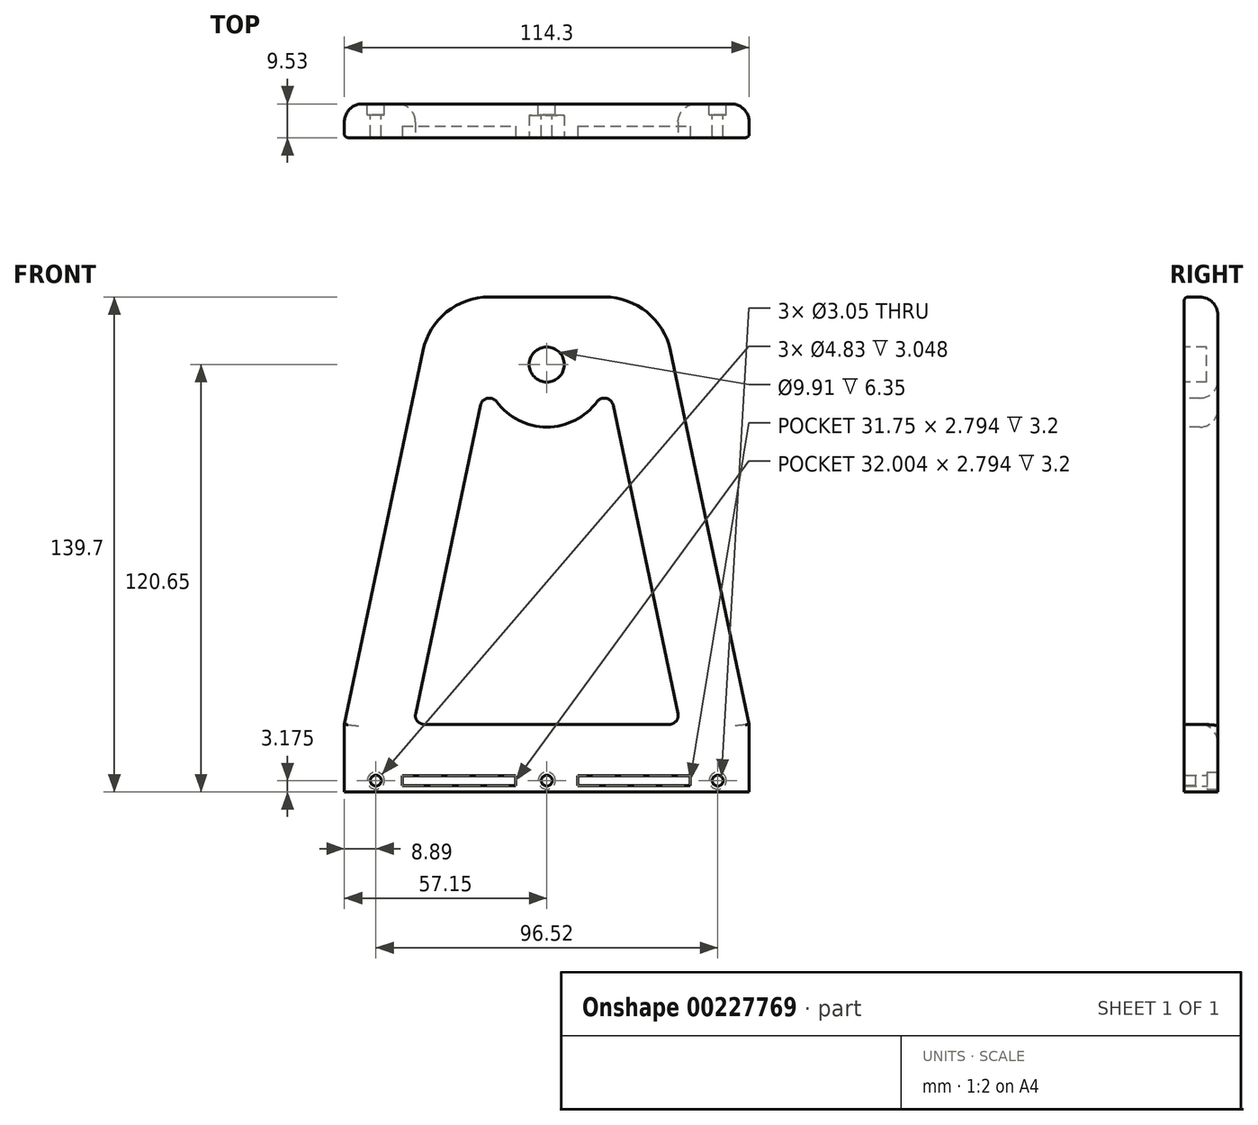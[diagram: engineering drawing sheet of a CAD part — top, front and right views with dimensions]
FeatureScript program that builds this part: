
annotation { "Feature Type Name" : "Feature", "Feature Type Description" : "" }
export const myFeature = defineFeature(function(context is Context, id is Id, definition is map)
    precondition{}
    {
        {
            var Q0;
            Q0=qCreatedBy(makeId("Front.planeOp"),FACE);
            var sketch = newSketch(context, id + "F0", { "sketchPlane" : qUnion([Q0])});
            skLineSegment(sketch, "E0", {"start": v(-57.15, 0) * mm, "end": v(57.15, 0) * mm});
            skLineSegment(sketch, "E1", {"start": v(57.15, 0) * mm, "end": v(57.15, 19.05) * mm});
            skLineSegment(sketch, "E2", {"start": v(57.15, 19.05) * mm, "end": v(31.75, 139.7) * mm});
            skLineSegment(sketch, "E3", {"start": v(31.75, 139.7) * mm, "end": v(-31.75, 139.7) * mm});
            skLineSegment(sketch, "E4", {"start": v(-57.15, 0) * mm, "end": v(-57.15, 19.05) * mm});
            skLineSegment(sketch, "E5", {"start": v(-57.15, 19.05) * mm, "end": v(-31.75, 139.7) * mm});
            skSolve(sketch);
        }
        {
            var Q0;
            Q0=qSketchRegion(id+"F0",true);
            extrude(context, id + "F1", {"entities" : qUnion([Q0]), "depth" : 9.52 * mm});
        }
        {
            var Q0;
            Q0=makeQuery(id+"F1.opExtrude","CAP_FACE",FACE,{"disambiguationData":[OSD([sQuery(id+"F0.wireOp",EDGE,"E0"),sQuery(id+"F0.wireOp",EDGE,"E1"),sQuery(id+"F0.wireOp",EDGE,"E2"),sQuery(id+"F0.wireOp",EDGE,"E3"),sQuery(id+"F0.wireOp",EDGE,"E4"),sQuery(id+"F0.wireOp",EDGE,"E5")])],"isStart":false});
            var sketch = newSketch(context, id + "F2", { "sketchPlane" : qUnion([Q0])});
            skCircle(sketch, "E6", {"center": v(0, 120.65) * mm, "radius": 4.95 * mm});
            skPoint(sketch, "E6.centerSnap0", {"position": v(0, 139.7) * mm});
            skSolve(sketch);
        }
        {
            var Q0;
            Q0=qSketchRegion(id+"F2",true);
            extrude(context, id + "F3", {"entities" : qUnion([Q0]), "operationType" : NewBodyOperationType.REMOVE, "oppositeDirection" : true, "depth" : 6.35 * mm});
        }
        {
            var Q0;
            Q0=makeQuery(id+"F1.opExtrude","SWEPT_EDGE",EDGE,{"disambiguationData":[OSD([sQuery(id+"F0.wireOp",EDGE,"E2"),sQuery(id+"F0.wireOp",EDGE,"E3")])]});
            var Q1;
            Q1=makeQuery(id+"F1.opExtrude","SWEPT_EDGE",EDGE,{"disambiguationData":[OSD([sQuery(id+"F0.wireOp",EDGE,"E3"),sQuery(id+"F0.wireOp",EDGE,"E5")])]});
            fillet(context, id + "F4", {"entities" : qUnion([Q0, Q1]), "radius" : 19.05 * mm, "tangentPropagation" : true, "allowEdgeOverflow" : false});
        }
        {
            var Q0;
            Q0=makeQuery(id+"F1.opExtrude","CAP_FACE",FACE,{"disambiguationData":[OSD([sQuery(id+"F0.wireOp",EDGE,"E0"),sQuery(id+"F0.wireOp",EDGE,"E1"),sQuery(id+"F0.wireOp",EDGE,"E2"),sQuery(id+"F0.wireOp",EDGE,"E3"),sQuery(id+"F0.wireOp",EDGE,"E4"),sQuery(id+"F0.wireOp",EDGE,"E5")])],"isStart":false});
            var sketch = newSketch(context, id + "F5", { "sketchPlane" : qUnion([Q0])});
            skArc(sketch, "E7", {"start": v(-14.19, 110.14) * mm, "mid": v(0, 103) * mm, "end": v(14.19, 110.14) * mm});
            skLineSegment(sketch, "E8", {"start": v(-34.55, 19.05) * mm, "end": v(34.55, 19.05) * mm});
            skLineSegment(sketch, "E9", {"start": v(37.04, 22.11) * mm, "end": v(18.71, 109.16) * mm});
            skLineSegment(sketch, "E10", {"start": v(-37.04, 22.11) * mm, "end": v(-18.71, 109.16) * mm});
            skPoint(sketch, "E11.visualSharp", {"position": v(-17.16, 116.52) * mm});
            skArc(sketch, "E11.filletArc", {"start": v(-14.19, 110.14) * mm, "mid": v(-16.77, 111.11) * mm, "end": v(-18.71, 109.16) * mm});
            skPoint(sketch, "E12.visualSharp", {"position": v(17.16, 116.52) * mm});
            skArc(sketch, "E12.filletArc", {"start": v(18.71, 109.16) * mm, "mid": v(16.77, 111.11) * mm, "end": v(14.19, 110.14) * mm});
            skPoint(sketch, "E13.visualSharp", {"position": v(37.68, 19.05) * mm});
            skArc(sketch, "E13.filletArc", {"start": v(34.55, 19.05) * mm, "mid": v(36.52, 19.99) * mm, "end": v(37.04, 22.11) * mm});
            skPoint(sketch, "E14.visualSharp", {"position": v(-37.68, 19.05) * mm});
            skArc(sketch, "E14.filletArc", {"start": v(-37.04, 22.11) * mm, "mid": v(-36.52, 19.99) * mm, "end": v(-34.55, 19.05) * mm});
            skSolve(sketch);
        }
        {
            var Q0;
            Q0=makeQuery(id+"F5.imprint","IMPRINT",FACE,{"disambiguationData":[TD([[makeQuery(id+"F5.imprint","IMPRINT",EDGE,{"derivedFrom":sQuery(id+"F5.wireOp",EDGE,"E7")}),-1.0]])]});
            extrude(context, id + "F6", {"entities" : qUnion([Q0]), "operationType" : NewBodyOperationType.REMOVE, "oppositeDirection" : true, "depth" : 25.4 * mm});
        }
        {
            var Q0;
            {var subQ0=sQuery(id+"F0.wireOp",EDGE,"E5");var subQ1=sQuery(id+"F0.wireOp",EDGE,"E3");Q0=makeQuery(id+"F4.opFillet","BLEND_EDGE",EDGE,{"blendedFrom":[makeQuery(id+"F1.opExtrude","SWEPT_EDGE",EDGE,{"disambiguationData":[OSD([subQ1,subQ0])]}),makeQuery(id+"F1.opExtrude","CAP_FACE",FACE,{"disambiguationData":[OSD([sQuery(id+"F0.wireOp",EDGE,"E0"),sQuery(id+"F0.wireOp",EDGE,"E1"),sQuery(id+"F0.wireOp",EDGE,"E2"),subQ1,sQuery(id+"F0.wireOp",EDGE,"E4"),subQ0])],"isStart":true})],"blendedInto":[makeQuery(id+"F1.opExtrude","CAP_FACE",FACE,{"disambiguationData":[OSD([sQuery(id+"F0.wireOp",EDGE,"E0"),sQuery(id+"F0.wireOp",EDGE,"E1"),sQuery(id+"F0.wireOp",EDGE,"E2"),subQ1,sQuery(id+"F0.wireOp",EDGE,"E4"),subQ0])],"isStart":true})]});}
            var Q1;
            Q1=makeQuery(id+"F1.opExtrude","CAP_EDGE",EDGE,{"disambiguationData":[OSD([sQuery(id+"F0.wireOp",EDGE,"E4")])],"isStart":true});
            var Q2;
            Q2=makeQuery(id+"F1.opExtrude","CAP_EDGE",EDGE,{"disambiguationData":[OSD([sQuery(id+"F0.wireOp",EDGE,"E1")])],"isStart":true});
            var Q3;
            Q3=makeQuery(id+"F6.boolean.opBoolean","INTERSECT",EDGE,{"derivedFrom":[makeQuery(id+"F1.opExtrude","CAP_FACE",FACE,{"disambiguationData":[OSD([sQuery(id+"F0.wireOp",EDGE,"E0"),sQuery(id+"F0.wireOp",EDGE,"E1"),sQuery(id+"F0.wireOp",EDGE,"E2"),sQuery(id+"F0.wireOp",EDGE,"E3"),sQuery(id+"F0.wireOp",EDGE,"E4"),sQuery(id+"F0.wireOp",EDGE,"E5")])],"isStart":true}),makeQuery(id+"F6.opExtrude","SWEPT_FACE",FACE,{"disambiguationData":[OSD([sQuery(id+"F5.wireOp",EDGE,"E7")])]})]});
            fillet(context, id + "F7", {"entities" : qUnion([Q0, Q1, Q2, Q3]), "radius" : 5.08 * mm, "tangentPropagation" : true, "allowEdgeOverflow" : false});
        }
        {
            var Q0;
            Q0=makeQuery(id+"F1.opExtrude","CAP_EDGE",EDGE,{"disambiguationData":[OSD([sQuery(id+"F0.wireOp",EDGE,"E1")])],"isStart":false});
            var Q1;
            Q1=makeQuery(id+"F1.opExtrude","CAP_EDGE",EDGE,{"disambiguationData":[OSD([sQuery(id+"F0.wireOp",EDGE,"E2")])],"isStart":false});
            var Q2;
            Q2=makeQuery(id+"F6.boolean.opBoolean","COPY",EDGE,{"derivedFrom":makeQuery(id+"F6.opExtrude","CAP_EDGE",EDGE,{"disambiguationData":[OSD([sQuery(id+"F5.wireOp",EDGE,"E10")])],"isStart":true})});
            var Q3;
            Q3=makeQuery(id+"F3.boolean.opBoolean","COPY",EDGE,{"derivedFrom":makeQuery(id+"F3.opExtrude","CAP_EDGE",EDGE,{"disambiguationData":[OSD([sQuery(id+"F2.wireOp",EDGE,"E6")])],"isStart":true})});
            var Q4;
            Q4=makeQuery(id+"F1.opExtrude","CAP_EDGE",EDGE,{"disambiguationData":[OSD([sQuery(id+"F0.wireOp",EDGE,"E4")])],"isStart":false});
            fillet(context, id + "F8", {"entities" : qUnion([Q0, Q1, Q2, Q3, Q4]), "radius" : 1.02 * mm, "tangentPropagation" : true, "allowEdgeOverflow" : false});
        }
        {
            var Q0;
            Q0=makeQuery(id+"F1.opExtrude","CAP_FACE",FACE,{"disambiguationData":[OSD([sQuery(id+"F0.wireOp",EDGE,"E0"),sQuery(id+"F0.wireOp",EDGE,"E1"),sQuery(id+"F0.wireOp",EDGE,"E2"),sQuery(id+"F0.wireOp",EDGE,"E3"),sQuery(id+"F0.wireOp",EDGE,"E4"),sQuery(id+"F0.wireOp",EDGE,"E5")])],"isStart":true});
            var sketch = newSketch(context, id + "F9", { "sketchPlane" : qUnion([Q0])});
            skCircle(sketch, "E15", {"center": v(0, 3.18) * mm, "radius": 1.52 * mm});
            skCircle(sketch, "E16", {"center": v(48.26, 3.18) * mm, "radius": 1.52 * mm});
            skCircle(sketch, "E17", {"center": v(-48.26, 3.18) * mm, "radius": 1.52 * mm});
            skSolve(sketch);
        }
        {
            var Q0;
            Q0 = qSketchRegion(id + "F9", true);
            extrude(context, id + "F10", {"entities" : qUnion([Q0]), "operationType" : NewBodyOperationType.REMOVE, "oppositeDirection" : true, "depth" : 25.4 * mm});
        }
        {
            var Q0;
            Q0=makeQuery(id+"F1.opExtrude","CAP_FACE",FACE,{"disambiguationData":[OSD([sQuery(id+"F0.wireOp",EDGE,"E0"),sQuery(id+"F0.wireOp",EDGE,"E1"),sQuery(id+"F0.wireOp",EDGE,"E2"),sQuery(id+"F0.wireOp",EDGE,"E3"),sQuery(id+"F0.wireOp",EDGE,"E4"),sQuery(id+"F0.wireOp",EDGE,"E5")])],"isStart":true});
            var sketch = newSketch(context, id + "F11", { "sketchPlane" : qUnion([Q0])});
            skCircle(sketch, "E18", {"center": v(-48.26, 3.18) * mm, "radius": 2.41 * mm});
            skCircle(sketch, "E19", {"center": v(0, 3.18) * mm, "radius": 2.41 * mm});
            skCircle(sketch, "E20", {"center": v(48.26, 3.18) * mm, "radius": 2.41 * mm});
            skSolve(sketch);
        }
        {
            var Q0;
            Q0 = qSketchRegion(id + "F11", true);
            extrude(context, id + "F12", {"entities" : qUnion([Q0]), "operationType" : NewBodyOperationType.REMOVE, "oppositeDirection" : true, "depth" : 3.05 * mm});
        }
        {
            var Q0;
            Q0=makeQuery(id+"F12.boolean.opBoolean","INTERSECT",EDGE,{"derivedFrom":[makeQuery(id+"F10.boolean.opBoolean","COPY",FACE,{"derivedFrom":makeQuery(id+"F10.opExtrude","SWEPT_FACE",FACE,{"disambiguationData":[OSD([sQuery(id+"F9.wireOp",EDGE,"E17")])]})}),makeQuery(id+"F12.opExtrude","CAP_FACE",FACE,{"disambiguationData":[OSD([sQuery(id+"F11.wireOp",EDGE,"E18")])],"isStart":false})]});
            var Q1;
            Q1=makeQuery(id+"F12.boolean.opBoolean","INTERSECT",EDGE,{"derivedFrom":[makeQuery(id+"F10.boolean.opBoolean","COPY",FACE,{"derivedFrom":makeQuery(id+"F10.opExtrude","SWEPT_FACE",FACE,{"disambiguationData":[OSD([sQuery(id+"F9.wireOp",EDGE,"E15")])]})}),makeQuery(id+"F12.opExtrude","CAP_FACE",FACE,{"disambiguationData":[OSD([sQuery(id+"F11.wireOp",EDGE,"E19")])],"isStart":false})]});
            var Q2;
            Q2=makeQuery(id+"F12.boolean.opBoolean","INTERSECT",EDGE,{"derivedFrom":[makeQuery(id+"F10.boolean.opBoolean","COPY",FACE,{"derivedFrom":makeQuery(id+"F10.opExtrude","SWEPT_FACE",FACE,{"disambiguationData":[OSD([sQuery(id+"F9.wireOp",EDGE,"E16")])]})}),makeQuery(id+"F12.opExtrude","CAP_FACE",FACE,{"disambiguationData":[OSD([sQuery(id+"F11.wireOp",EDGE,"E20")])],"isStart":false})]});
            fillet(context, id + "F13", {"entities" : qUnion([Q0, Q1, Q2]), "radius" : 0.25 * mm, "tangentPropagation" : true, "allowEdgeOverflow" : false});
        }
        {
            var Q0;
            Q0=makeQuery(id+"F1.opExtrude","CAP_FACE",FACE,{"disambiguationData":[OSD([sQuery(id+"F0.wireOp",EDGE,"E0"),sQuery(id+"F0.wireOp",EDGE,"E1"),sQuery(id+"F0.wireOp",EDGE,"E2"),sQuery(id+"F0.wireOp",EDGE,"E3"),sQuery(id+"F0.wireOp",EDGE,"E4"),sQuery(id+"F0.wireOp",EDGE,"E5")])],"isStart":false});
            var sketch = newSketch(context, id + "F14", { "sketchPlane" : qUnion([Q0])});
            skLineSegment(sketch, "E21.bottom", {"start": v(-40.77, 4.57) * mm, "end": v(-8.76, 4.57) * mm});
            skLineSegment(sketch, "E21.top", {"start": v(-40.77, 1.78) * mm, "end": v(-8.76, 1.78) * mm});
            skLineSegment(sketch, "E21.left", {"start": v(-40.77, 4.57) * mm, "end": v(-40.77, 1.78) * mm});
            skLineSegment(sketch, "E21.right", {"start": v(-8.76, 4.57) * mm, "end": v(-8.76, 1.78) * mm});
            skLineSegment(sketch, "E22.bottom", {"start": v(8.76, 4.57) * mm, "end": v(40.51, 4.57) * mm});
            skLineSegment(sketch, "E22.top", {"start": v(8.76, 1.78) * mm, "end": v(40.51, 1.78) * mm});
            skLineSegment(sketch, "E22.left", {"start": v(8.76, 4.57) * mm, "end": v(8.76, 1.78) * mm});
            skLineSegment(sketch, "E22.right", {"start": v(40.51, 4.57) * mm, "end": v(40.51, 1.78) * mm});
            skSolve(sketch);
        }
        {
            var Q0;
            Q0 = qSketchRegion(id + "F14", true);
            extrude(context, id + "F15", {"entities" : qUnion([Q0]), "operationType" : NewBodyOperationType.REMOVE, "oppositeDirection" : true, "depth" : 3.2 * mm});
        }
        {
            var Q0;
            Q0=makeQuery(id+"F15.boolean.opBoolean","COPY",EDGE,{"derivedFrom":makeQuery(id+"F15.opExtrude","CAP_EDGE",EDGE,{"disambiguationData":[OSD([sQuery(id+"F14.wireOp",EDGE,"E21.bottom")])],"isStart":true})});
            var Q1;
            Q1=makeQuery(id+"F15.boolean.opBoolean","COPY",EDGE,{"derivedFrom":makeQuery(id+"F15.opExtrude","CAP_EDGE",EDGE,{"disambiguationData":[OSD([sQuery(id+"F14.wireOp",EDGE,"E21.left")])],"isStart":true})});
            var Q2;
            Q2=makeQuery(id+"F15.boolean.opBoolean","COPY",EDGE,{"derivedFrom":makeQuery(id+"F15.opExtrude","CAP_EDGE",EDGE,{"disambiguationData":[OSD([sQuery(id+"F14.wireOp",EDGE,"E21.top")])],"isStart":true})});
            var Q3;
            Q3=makeQuery(id+"F15.boolean.opBoolean","COPY",EDGE,{"derivedFrom":makeQuery(id+"F15.opExtrude","CAP_EDGE",EDGE,{"disambiguationData":[OSD([sQuery(id+"F14.wireOp",EDGE,"E21.right")])],"isStart":true})});
            var Q4;
            Q4=makeQuery(id+"F15.boolean.opBoolean","COPY",EDGE,{"derivedFrom":makeQuery(id+"F15.opExtrude","CAP_EDGE",EDGE,{"disambiguationData":[OSD([sQuery(id+"F14.wireOp",EDGE,"E22.bottom")])],"isStart":true})});
            var Q5;
            Q5=makeQuery(id+"F15.boolean.opBoolean","COPY",EDGE,{"derivedFrom":makeQuery(id+"F15.opExtrude","CAP_EDGE",EDGE,{"disambiguationData":[OSD([sQuery(id+"F14.wireOp",EDGE,"E22.left")])],"isStart":true})});
            var Q6;
            Q6=makeQuery(id+"F15.boolean.opBoolean","COPY",EDGE,{"derivedFrom":makeQuery(id+"F15.opExtrude","CAP_EDGE",EDGE,{"disambiguationData":[OSD([sQuery(id+"F14.wireOp",EDGE,"E22.top")])],"isStart":true})});
            var Q7;
            Q7=makeQuery(id+"F15.boolean.opBoolean","COPY",EDGE,{"derivedFrom":makeQuery(id+"F15.opExtrude","CAP_EDGE",EDGE,{"disambiguationData":[OSD([sQuery(id+"F14.wireOp",EDGE,"E22.right")])],"isStart":true})});
            var Q8;
            Q8=makeQuery(id+"F10.boolean.opBoolean","INTERSECT",EDGE,{"derivedFrom":[makeQuery(id+"F1.opExtrude","CAP_FACE",FACE,{"disambiguationData":[OSD([sQuery(id+"F0.wireOp",EDGE,"E0"),sQuery(id+"F0.wireOp",EDGE,"E1"),sQuery(id+"F0.wireOp",EDGE,"E2"),sQuery(id+"F0.wireOp",EDGE,"E3"),sQuery(id+"F0.wireOp",EDGE,"E4"),sQuery(id+"F0.wireOp",EDGE,"E5")])],"isStart":false}),makeQuery(id+"F10.opExtrude","SWEPT_FACE",FACE,{"disambiguationData":[OSD([sQuery(id+"F9.wireOp",EDGE,"E16")])]})]});
            var Q9;
            Q9=makeQuery(id+"F10.boolean.opBoolean","INTERSECT",EDGE,{"derivedFrom":[makeQuery(id+"F1.opExtrude","CAP_FACE",FACE,{"disambiguationData":[OSD([sQuery(id+"F0.wireOp",EDGE,"E0"),sQuery(id+"F0.wireOp",EDGE,"E1"),sQuery(id+"F0.wireOp",EDGE,"E2"),sQuery(id+"F0.wireOp",EDGE,"E3"),sQuery(id+"F0.wireOp",EDGE,"E4"),sQuery(id+"F0.wireOp",EDGE,"E5")])],"isStart":false}),makeQuery(id+"F10.opExtrude","SWEPT_FACE",FACE,{"disambiguationData":[OSD([sQuery(id+"F9.wireOp",EDGE,"E15")])]})]});
            var Q10;
            Q10=makeQuery(id+"F10.boolean.opBoolean","INTERSECT",EDGE,{"derivedFrom":[makeQuery(id+"F1.opExtrude","CAP_FACE",FACE,{"disambiguationData":[OSD([sQuery(id+"F0.wireOp",EDGE,"E0"),sQuery(id+"F0.wireOp",EDGE,"E1"),sQuery(id+"F0.wireOp",EDGE,"E2"),sQuery(id+"F0.wireOp",EDGE,"E3"),sQuery(id+"F0.wireOp",EDGE,"E4"),sQuery(id+"F0.wireOp",EDGE,"E5")])],"isStart":false}),makeQuery(id+"F10.opExtrude","SWEPT_FACE",FACE,{"disambiguationData":[OSD([sQuery(id+"F9.wireOp",EDGE,"E17")])]})]});
            fillet(context, id + "F16", {"entities" : qUnion([Q0, Q1, Q2, Q3, Q4, Q5, Q6, Q7, Q8, Q9, Q10]), "radius" : 0.5 * mm, "tangentPropagation" : true, "allowEdgeOverflow" : false});
        }
    });
